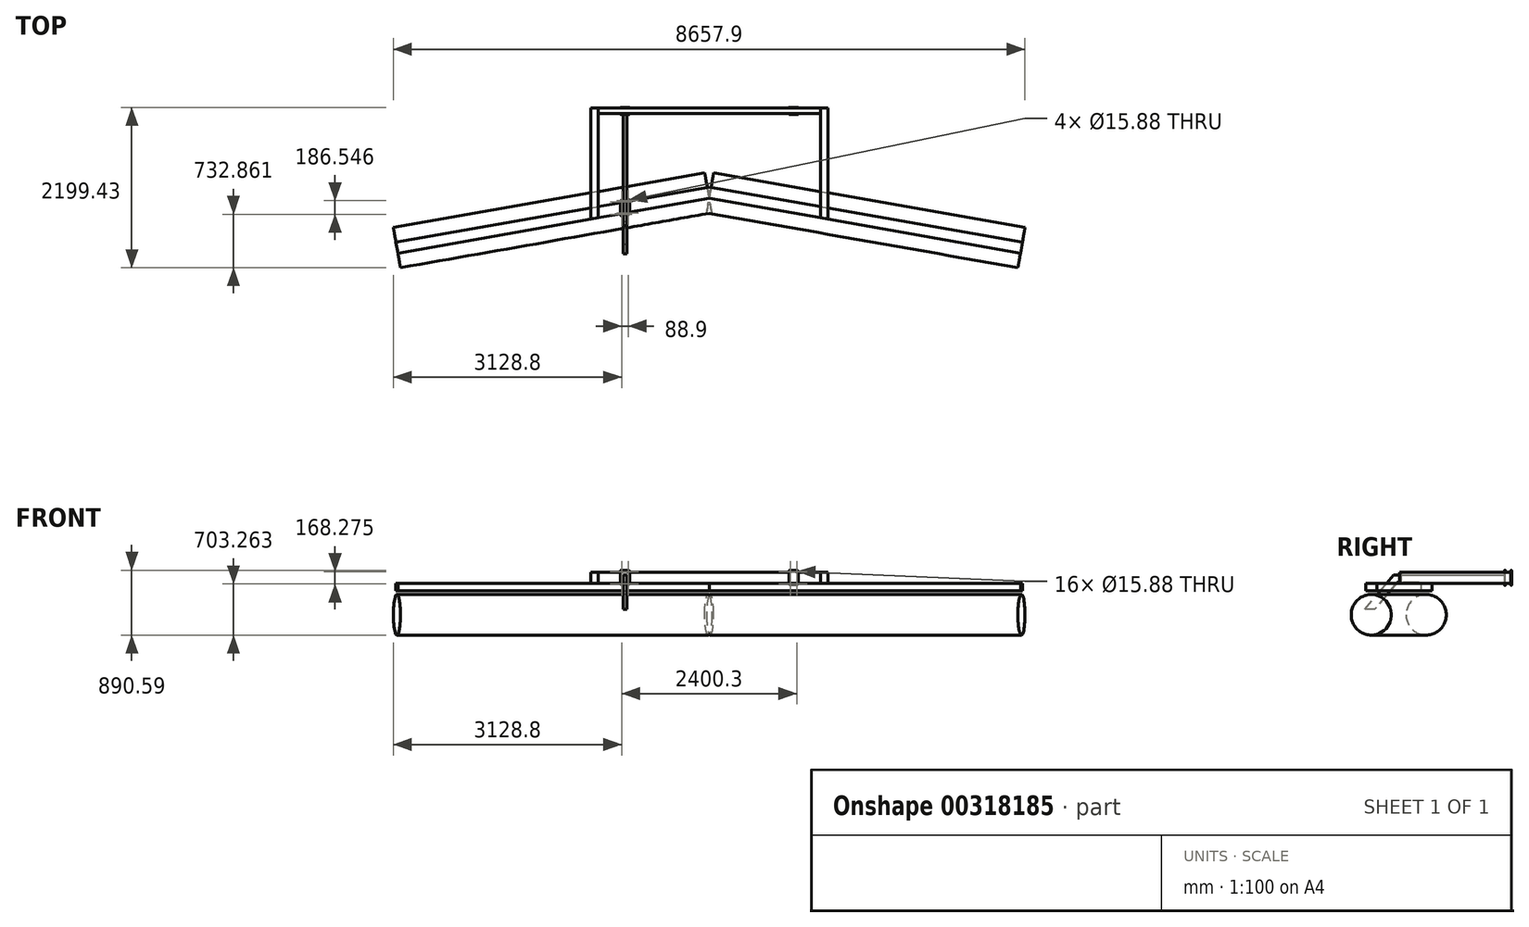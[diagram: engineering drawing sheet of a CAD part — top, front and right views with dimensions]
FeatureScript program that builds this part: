
annotation { "Feature Type Name" : "Feature", "Feature Type Description" : "" }
export const myFeature = defineFeature(function(context is Context, id is Id, definition is map)
    precondition{}
    {
        {
            var Q0;
            Q0=qCreatedBy(makeId("Top.planeOp"),FACE);
            var sketch = newSketch(context, id + "F0", { "sketchPlane" : qUnion([Q0])});
            skLineSegment(sketch, "E0", {"start": v(-4267.2, -752.42) * mm, "end": v(0, 0) * mm});
            skLineSegment(sketch, "E1", {"start": v(0, 0) * mm, "end": v(4267.2, -752.42) * mm});
            skLineSegment(sketch, "E2", {"start": v(-4267.2, -752.42) * mm, "end": v(-4293.66, -602.34) * mm});
            skLineSegment(sketch, "E3", {"start": v(-4293.66, -602.34) * mm, "end": v(0, 154.75) * mm});
            skLineSegment(sketch, "E4", {"start": v(0, 154.75) * mm, "end": v(4293.66, -602.34) * mm});
            skLineSegment(sketch, "E5", {"start": v(4267.2, -752.42) * mm, "end": v(4293.66, -602.34) * mm});
            skLineSegment(sketch, "E6", {"start": v(0, 0) * mm, "end": v(0, -830.88) * mm, "construction": true});
            skSolve(sketch);
        }
        {
            var Q0;
            Q0=makeQuery(id+"F0.imprint","IMPRINT",FACE,{"disambiguationData":[TD([[makeQuery(id+"F0.imprint","IMPRINT",EDGE,{"derivedFrom":sQuery(id+"F0.wireOp",EDGE,"E0")}),1.0]])]});
            extrude(context, id + "F1", {"entities" : qUnion([Q0]), "depth" : 101.6 * mm});
        }
        {
            var Q0;
            Q0=makeQuery(id+"F1.opExtrude","CAP_FACE",FACE,{"disambiguationData":[OSD([sQuery(id+"F0.wireOp",EDGE,"E0"),sQuery(id+"F0.wireOp",EDGE,"E1"),sQuery(id+"F0.wireOp",EDGE,"E2"),sQuery(id+"F0.wireOp",EDGE,"E3"),sQuery(id+"F0.wireOp",EDGE,"E4"),sQuery(id+"F0.wireOp",EDGE,"E5")])],"isStart":false});
            var sketch = newSketch(context, id + "F2", { "sketchPlane" : qUnion([Q0])});
            skLineSegment(sketch, "E7", {"start": v(1524, -268.72) * mm, "end": v(1524, 1237.36) * mm});
            skLineSegment(sketch, "E8", {"start": v(1524, 1237.36) * mm, "end": v(1625.6, 1237.36) * mm});
            skLineSegment(sketch, "E9", {"start": v(1625.6, 1237.36) * mm, "end": v(1625.6, -286.64) * mm});
            skLineSegment(sketch, "E10", {"start": v(1625.6, -286.64) * mm, "end": v(1524, -268.72) * mm});
            skSolve(sketch);
        }
        {
            var Q0;
            {var subQ0=sQuery(id+"F2.wireOp",EDGE,"E8");Q0=makeQuery(id+"F2.imprint","IMPRINT",FACE,{"disambiguationData":[TD([[makeQuery(id+"F2.imprint","IMPRINT",EDGE,{"derivedFrom":subQ0}),-1.0]])]});}
            var Q1;
            {var subQ0=sQuery(id+"F2.wireOp",EDGE,"E10");Q1=makeQuery(id+"F2.imprint","IMPRINT",FACE,{"disambiguationData":[TD([[makeQuery(id+"F2.imprint","IMPRINT",EDGE,{"derivedFrom":subQ0}),1.0]])]});}
            extrude(context, id + "F3", {"entities" : qUnion([Q0, Q1]), "depth" : 152.4 * mm});
        }
        {
            var Q0;
            Q0=makeQuery(id+"F3.opExtrude","SWEPT_BODY",BODY,{"disambiguationData":[OSD([sQuery(id+"F2.wireOp",EDGE,"E7"),sQuery(id+"F2.wireOp",EDGE,"E8"),sQuery(id+"F2.wireOp",EDGE,"E9"),sQuery(id+"F2.wireOp",EDGE,"E10")])]});
            var Q1;
            Q1=qCreatedBy(makeId("Right.planeOp"),FACE);
            mirror(context, id + "F4", {"entities" : qUnion([Q0]), "mirrorPlane" : qUnion([Q1])});
        }
        {
            var Q0;
            Q0=makeQuery(id+"F4.opPattern","COPY",FACE,{"derivedFrom":makeQuery(id+"F3.opExtrude","SWEPT_FACE",FACE,{"disambiguationData":[OSD([sQuery(id+"F2.wireOp",EDGE,"E7")])]}),"instanceName":"1"});
            var sketch = newSketch(context, id + "F5", { "sketchPlane" : qUnion([Q0])});
            skLineSegment(sketch, "E11.bottom", {"start": v(1237.36, 254) * mm, "end": v(1161.16, 254) * mm});
            skLineSegment(sketch, "E11.top", {"start": v(1237.36, 101.6) * mm, "end": v(1161.16, 101.6) * mm});
            skLineSegment(sketch, "E11.left", {"start": v(1237.36, 254) * mm, "end": v(1237.36, 101.6) * mm});
            skLineSegment(sketch, "E11.right", {"start": v(1161.16, 254) * mm, "end": v(1161.16, 101.6) * mm});
            skSolve(sketch);
        }
        {
            var Q0;
            Q0 = qSketchRegion(id + "F5", true);
            extrude(context, id + "F6", {"entities" : qUnion([Q0]), "endBound" : BoundingType.UP_TO_NEXT, "depth" : 25.4 * mm});
        }
        {
            var Q0;
            Q0=makeQuery(id+"F6.opExtrude","SWEPT_FACE",FACE,{"disambiguationData":[OSD([sQuery(id+"F5.wireOp",EDGE,"E11.right")])]});
            var sketch = newSketch(context, id + "F7", { "sketchPlane" : qUnion([Q0])});
            skLineSegment(sketch, "E12.bottom", {"start": v(-1108.08, 74.61) * mm, "end": v(-1203.33, 74.61) * mm});
            skLineSegment(sketch, "E12.top", {"start": v(-1108.08, 280.99) * mm, "end": v(-1203.33, 280.99) * mm});
            skLineSegment(sketch, "E12.left", {"start": v(-1092.2, 90.49) * mm, "end": v(-1092.2, 265.11) * mm});
            skLineSegment(sketch, "E12.right", {"start": v(-1219.2, 90.49) * mm, "end": v(-1219.2, 265.11) * mm});
            skPoint(sketch, "E12.centerSnap0", {"position": v(-1524, 177.8) * mm});
            skCircle(sketch, "E13", {"center": v(-1200.15, 261.94) * mm, "radius": 7.94 * mm});
            skCircle(sketch, "E14", {"center": v(-1111.25, 261.94) * mm, "radius": 7.94 * mm});
            skLineSegment(sketch, "E15", {"start": v(-1219.2, 261.94) * mm, "end": v(-1092.2, 261.94) * mm, "construction": true});
            skCircle(sketch, "E16", {"center": v(-1200.15, 93.66) * mm, "radius": 7.94 * mm});
            skCircle(sketch, "E17", {"center": v(-1111.25, 93.66) * mm, "radius": 7.94 * mm});
            skLineSegment(sketch, "E18", {"start": v(-1219.2, 93.66) * mm, "end": v(-1117.6, 93.66) * mm, "construction": true});
            skLineSegment(sketch, "E19", {"start": v(-1200.15, 261.94) * mm, "end": v(-1200.15, 93.66) * mm, "construction": true});
            skLineSegment(sketch, "E20", {"start": v(-1111.25, 261.94) * mm, "end": v(-1111.25, 93.66) * mm, "construction": true});
            skPoint(sketch, "E21.visualSharp", {"position": v(-1219.2, 280.99) * mm});
            skArc(sketch, "E21.filletArc", {"start": v(-1203.33, 280.99) * mm, "mid": v(-1214.55, 276.34) * mm, "end": v(-1219.2, 265.11) * mm});
            skPoint(sketch, "E22.visualSharp", {"position": v(-1092.2, 280.99) * mm});
            skArc(sketch, "E22.filletArc", {"start": v(-1092.2, 265.11) * mm, "mid": v(-1096.85, 276.34) * mm, "end": v(-1108.08, 280.99) * mm});
            skPoint(sketch, "E23.visualSharp", {"position": v(-1092.2, 74.61) * mm});
            skArc(sketch, "E23.filletArc", {"start": v(-1108.08, 74.61) * mm, "mid": v(-1096.85, 79.26) * mm, "end": v(-1092.2, 90.49) * mm});
            skPoint(sketch, "E24.visualSharp", {"position": v(-1219.2, 74.61) * mm});
            skArc(sketch, "E24.filletArc", {"start": v(-1219.2, 90.49) * mm, "mid": v(-1214.55, 79.26) * mm, "end": v(-1203.33, 74.61) * mm});
            skSolve(sketch);
        }
        {
            var Q0;
            Q0 = qSketchRegion(id + "F7", true);
            extrude(context, id + "F8", {"entities" : qUnion([Q0]), "depth" : 9.52 * mm});
        }
        {
            var Q0;
            Q0=makeQuery(id+"F6.opExtrude","SWEPT_FACE",FACE,{"disambiguationData":[OSD([sQuery(id+"F5.wireOp",EDGE,"E11.right")])]});
            cPlane(context, id + "F9", {"entities" : qUnion([Q0]), "cplaneType" : CPlaneType.OFFSET, "offset" : 38.1 * mm, "oppositeDirection" : true, "width" : 152.4 * mm, "height" : 152.4 * mm});
        }
        {
            var Q0;
            Q0=makeQuery(id+"F8.opExtrude","SWEPT_BODY",BODY,{"disambiguationData":[OSD([sQuery(id+"F7.wireOp",EDGE,"E12.bottom"),sQuery(id+"F7.wireOp",EDGE,"E12.top"),sQuery(id+"F7.wireOp",EDGE,"E12.left"),sQuery(id+"F7.wireOp",EDGE,"E12.right"),sQuery(id+"F7.wireOp",EDGE,"E13"),sQuery(id+"F7.wireOp",EDGE,"E14"),sQuery(id+"F7.wireOp",EDGE,"E16"),sQuery(id+"F7.wireOp",EDGE,"E17"),sQuery(id+"F7.wireOp",EDGE,"E21.filletArc"),sQuery(id+"F7.wireOp",EDGE,"E22.filletArc"),sQuery(id+"F7.wireOp",EDGE,"E23.filletArc"),sQuery(id+"F7.wireOp",EDGE,"E24.filletArc")])]});
            var Q1;
            Q1=qCreatedBy(id+"F9.planeOp",FACE);
            mirror(context, id + "F10", {"entities" : qUnion([Q0]), "mirrorPlane" : qUnion([Q1])});
        }
        {
            var Q0;
            Q0=makeQuery(id+"F8.opExtrude","SWEPT_BODY",BODY,{"disambiguationData":[OSD([sQuery(id+"F7.wireOp",EDGE,"E12.bottom"),sQuery(id+"F7.wireOp",EDGE,"E12.top"),sQuery(id+"F7.wireOp",EDGE,"E12.left"),sQuery(id+"F7.wireOp",EDGE,"E12.right"),sQuery(id+"F7.wireOp",EDGE,"E13"),sQuery(id+"F7.wireOp",EDGE,"E14"),sQuery(id+"F7.wireOp",EDGE,"E16"),sQuery(id+"F7.wireOp",EDGE,"E17"),sQuery(id+"F7.wireOp",EDGE,"E21.filletArc"),sQuery(id+"F7.wireOp",EDGE,"E22.filletArc"),sQuery(id+"F7.wireOp",EDGE,"E23.filletArc"),sQuery(id+"F7.wireOp",EDGE,"E24.filletArc")])]});
            var Q1;
            Q1=makeQuery(id+"F10.opPattern","COPY",BODY,{"derivedFrom":makeQuery(id+"F8.opExtrude","SWEPT_BODY",BODY,{"disambiguationData":[OSD([sQuery(id+"F7.wireOp",EDGE,"E12.bottom"),sQuery(id+"F7.wireOp",EDGE,"E12.top"),sQuery(id+"F7.wireOp",EDGE,"E12.left"),sQuery(id+"F7.wireOp",EDGE,"E12.right"),sQuery(id+"F7.wireOp",EDGE,"E13"),sQuery(id+"F7.wireOp",EDGE,"E14"),sQuery(id+"F7.wireOp",EDGE,"E16"),sQuery(id+"F7.wireOp",EDGE,"E17"),sQuery(id+"F7.wireOp",EDGE,"E21.filletArc"),sQuery(id+"F7.wireOp",EDGE,"E22.filletArc"),sQuery(id+"F7.wireOp",EDGE,"E23.filletArc"),sQuery(id+"F7.wireOp",EDGE,"E24.filletArc")])]}),"instanceName":"1"});
            var Q2;
            Q2=qCreatedBy(makeId("Right.planeOp"),FACE);
            mirror(context, id + "F11", {"entities" : qUnion([Q0, Q1]), "mirrorPlane" : qUnion([Q2])});
        }
        {
            var Q0;
            {var subQ1=makeQuery(id+"F1.opExtrude","CAP_EDGE",EDGE,{"disambiguationData":[OSD([sQuery(id+"F0.wireOp",EDGE,"E0")])],"isStart":false});Q0=makeQuery(id+"F2.imprint","IMPRINT",FACE,{"disambiguationData":[TD([[makeQuery(id+"F2.imprint","IMPRINT",EDGE,{"derivedFrom":subQ1}),1.0]])]});}
            var sketch = newSketch(context, id + "F12", { "sketchPlane" : qUnion([Q0])});
            skLineSegment(sketch, "E25", {"start": v(-1219.2, -46.14) * mm, "end": v(-1219.2, -223.46) * mm});
            skLineSegment(sketch, "E26", {"start": v(-1200.57, -239.1) * mm, "end": v(-1105.32, -222.3) * mm});
            skLineSegment(sketch, "E27", {"start": v(-1206.08, -30.5) * mm, "end": v(-1110.83, -13.71) * mm});
            skLineSegment(sketch, "E28", {"start": v(-1092.2, -29.35) * mm, "end": v(-1092.2, -206.67) * mm});
            skLineSegment(sketch, "E29", {"start": v(-1219.2, -52.17) * mm, "end": v(-1092.2, -29.77) * mm, "construction": true});
            skLineSegment(sketch, "E30", {"start": v(-1219.2, -223.04) * mm, "end": v(-1092.2, -200.64) * mm, "construction": true});
            skLineSegment(sketch, "E31", {"start": v(-1200.15, -48.8) * mm, "end": v(-1200.15, -219.68) * mm, "construction": true});
            skLineSegment(sketch, "E32", {"start": v(-1111.25, -33.13) * mm, "end": v(-1111.25, -204) * mm, "construction": true});
            skCircle(sketch, "E33", {"center": v(-1200.15, -48.8) * mm, "radius": 7.94 * mm});
            skCircle(sketch, "E34", {"center": v(-1111.25, -33.13) * mm, "radius": 7.94 * mm});
            skCircle(sketch, "E35", {"center": v(-1200.15, -219.68) * mm, "radius": 7.94 * mm});
            skCircle(sketch, "E36", {"center": v(-1111.25, -204) * mm, "radius": 7.94 * mm});
            skPoint(sketch, "E37.visualSharp", {"position": v(-1219.2, -32.82) * mm});
            skArc(sketch, "E37.filletArc", {"start": v(-1206.08, -30.5) * mm, "mid": v(-1215.49, -35.94) * mm, "end": v(-1219.2, -46.14) * mm});
            skPoint(sketch, "E38.visualSharp", {"position": v(-1092.2, -10.43) * mm});
            skArc(sketch, "E38.filletArc", {"start": v(-1092.2, -29.35) * mm, "mid": v(-1097.87, -17.19) * mm, "end": v(-1110.83, -13.71) * mm});
            skPoint(sketch, "E39.visualSharp", {"position": v(-1092.2, -219.99) * mm});
            skArc(sketch, "E39.filletArc", {"start": v(-1105.32, -222.3) * mm, "mid": v(-1095.91, -216.87) * mm, "end": v(-1092.2, -206.67) * mm});
            skPoint(sketch, "E40.visualSharp", {"position": v(-1219.2, -242.38) * mm});
            skArc(sketch, "E40.filletArc", {"start": v(-1219.2, -223.46) * mm, "mid": v(-1213.53, -235.62) * mm, "end": v(-1200.57, -239.1) * mm});
            skSolve(sketch);
        }
        {
            var Q0;
            Q0 = qSketchRegion(id + "F12", true);
            extrude(context, id + "F13", {"entities" : qUnion([Q0]), "operationType" : NewBodyOperationType.ADD, "depth" : 9.52 * mm});
        }
        {
            var Q0;
            Q0=makeQuery(id+"F8.opExtrude","CAP_FACE",FACE,{"disambiguationData":[OSD([sQuery(id+"F7.wireOp",EDGE,"E12.bottom"),sQuery(id+"F7.wireOp",EDGE,"E12.top"),sQuery(id+"F7.wireOp",EDGE,"E12.left"),sQuery(id+"F7.wireOp",EDGE,"E12.right"),sQuery(id+"F7.wireOp",EDGE,"E13"),sQuery(id+"F7.wireOp",EDGE,"E14"),sQuery(id+"F7.wireOp",EDGE,"E16"),sQuery(id+"F7.wireOp",EDGE,"E17"),sQuery(id+"F7.wireOp",EDGE,"E21.filletArc"),sQuery(id+"F7.wireOp",EDGE,"E22.filletArc"),sQuery(id+"F7.wireOp",EDGE,"E23.filletArc"),sQuery(id+"F7.wireOp",EDGE,"E24.filletArc")])],"isStart":false});
            var sketch = newSketch(context, id + "F14", { "sketchPlane" : qUnion([Q0])});
            skLineSegment(sketch, "E41", {"start": v(-1130.3, 110.8) * mm, "end": v(-1181.1, 110.8) * mm});
            skLineSegment(sketch, "E42", {"start": v(-1181.1, 110.8) * mm, "end": v(-1181.1, 212.4) * mm});
            skLineSegment(sketch, "E43", {"start": v(-1181.1, 212.4) * mm, "end": v(-1130.3, 212.4) * mm});
            skLineSegment(sketch, "E44", {"start": v(-1130.3, 212.4) * mm, "end": v(-1130.3, 110.8) * mm});
            skLineSegment(sketch, "E45", {"start": v(-1155.7, 212.4) * mm, "end": v(-1155.7, 280.99) * mm, "construction": true});
            skSolve(sketch);
        }
        {
            var Q0;
            Q0=makeQuery(id+"F14.imprint","IMPRINT",FACE,{"disambiguationData":[TD([[makeQuery(id+"F14.imprint","IMPRINT",EDGE,{"derivedFrom":sQuery(id+"F14.wireOp",EDGE,"E41")}),-1.0]])]});
            extrude(context, id + "F15", {"entities" : qUnion([Q0]), "depth" : 1524 * mm});
        }
        {
            var Q0;
            Q0=makeQuery(id+"F15.opExtrude","SWEPT_FACE",FACE,{"disambiguationData":[OSD([sQuery(id+"F14.wireOp",EDGE,"E42")])]});
            var sketch = newSketch(context, id + "F16", { "sketchPlane" : qUnion([Q0])});
            skLineSegment(sketch, "E46", {"start": v(372.36, 212.4) * mm, "end": v(324.99, 110.8) * mm});
            skLineSegment(sketch, "E47", {"start": v(324.99, 110.8) * mm, "end": v(372.36, 110.8) * mm});
            skLineSegment(sketch, "E48", {"start": v(372.36, 110.8) * mm, "end": v(372.36, 212.4) * mm});
            skSolve(sketch);
        }
        {
            var Q0;
            Q0 = qSketchRegion(id + "F16", true);
            extrude(context, id + "F17", {"entities" : qUnion([Q0]), "operationType" : NewBodyOperationType.REMOVE, "endBound" : BoundingType.UP_TO_NEXT, "oppositeDirection" : true, "depth" : 25.4 * mm});
        }
        {
            var Q0;
            Q0=makeQuery(id+"F15.opExtrude","SWEPT_FACE",FACE,{"disambiguationData":[OSD([sQuery(id+"F14.wireOp",EDGE,"E42")])]});
            var sketch = newSketch(context, id + "F18", { "sketchPlane" : qUnion([Q0])});
            skLineSegment(sketch, "E49", {"start": v(324.99, 110.8) * mm, "end": v(631.58, -254.57) * mm});
            skLineSegment(sketch, "E50", {"start": v(631.58, -254.57) * mm, "end": v(764.2, -254.57) * mm});
            skLineSegment(sketch, "E51", {"start": v(764.2, -254.57) * mm, "end": v(372.36, 212.4) * mm});
            skLineSegment(sketch, "E52", {"start": v(372.36, 212.4) * mm, "end": v(324.99, 110.8) * mm});
            skSolve(sketch);
        }
        {
            var Q0;
            Q0 = qSketchRegion(id + "F18", true);
            var Q1;
            Q1=makeQuery(id+"F15.opExtrude","SWEPT_FACE",FACE,{"disambiguationData":[OSD([sQuery(id+"F14.wireOp",EDGE,"E44")])]});
            extrude(context, id + "F19", {"entities" : qUnion([Q0]), "operationType" : NewBodyOperationType.ADD, "endBound" : BoundingType.UP_TO_SURFACE, "oppositeDirection" : true, "endBoundEntityFace" : qUnion([Q1]), "depth" : 25.4 * mm});
        }
        {
            var Q0;
            Q0=makeQuery(id+"F1.opExtrude","SWEPT_FACE",FACE,{"disambiguationData":[OSD([sQuery(id+"F0.wireOp",EDGE,"E2")])]});
            var sketch = newSketch(context, id + "F20", { "sketchPlane" : qUnion([Q0])});
            skLineSegment(sketch, "E53", {"start": v(-76.2, 0) * mm, "end": v(-76.2, -609.6) * mm});
            skCircle(sketch, "E54", {"center": v(-76.2, -330.2) * mm, "radius": 279.4 * mm});
            skSolve(sketch);
        }
        {
            var Q0;
            Q0 = qSketchRegion(id + "F20", true);
            var Q1;
            Q1=qCreatedBy(makeId("Origin.pointOp"),VERTEX);
            extrude(context, id + "F21", {"entities" : qUnion([Q0]), "endBound" : BoundingType.UP_TO_VERTEX, "oppositeDirection" : true, "endBoundEntityVertex" : qUnion([Q1]), "depth" : 25.4 * mm});
        }
        {
            var Q0;
            Q0=makeQuery(id+"F21.opExtrude","SWEPT_BODY",BODY,{"disambiguationData":[OSD([sQuery(id+"F20.wireOp",EDGE,"E54")])]});
            var Q1;
            Q1=qCreatedBy(makeId("Right.planeOp"),FACE);
            mirror(context, id + "F22", {"operationType" : NewBodyOperationType.ADD, "entities" : qUnion([Q0]), "mirrorPlane" : qUnion([Q1])});
        }
    });
